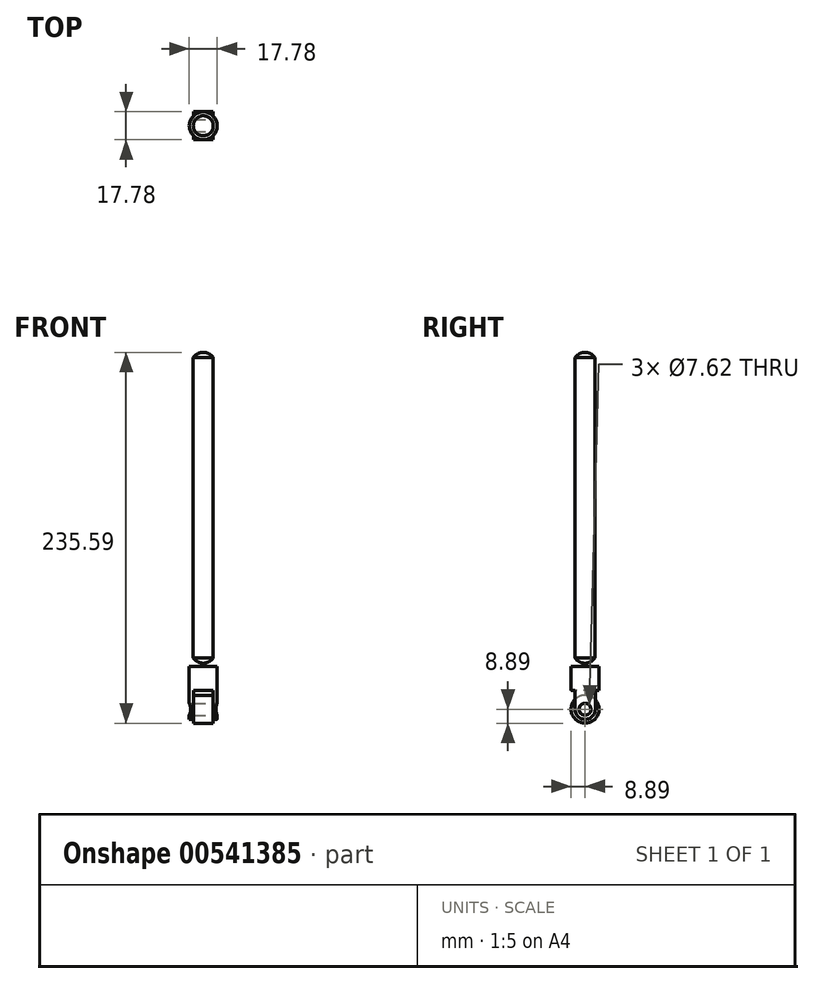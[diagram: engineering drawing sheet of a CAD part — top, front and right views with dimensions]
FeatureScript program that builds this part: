
annotation { "Feature Type Name" : "Feature", "Feature Type Description" : "" }
export const myFeature = defineFeature(function(context is Context, id is Id, definition is map)
    precondition{}
    {
        {
            var Q0;
            Q0=qCreatedBy(makeId("Top.planeOp"),FACE);
            var sketch = newSketch(context, id + "F0", { "sketchPlane" : qUnion([Q0])});
            skCircle(sketch, "E0", {"center": v(0, 0) * mm, "radius": 8.9 * mm});
            skSolve(sketch);
        }
        {
            var Q0;
            Q0=makeQuery(id+"F0.imprint","IMPRINT",FACE,{"disambiguationData":[TD([[makeQuery(id+"F0.imprint","IMPRINT",EDGE,{"derivedFrom":sQuery(id+"F0.wireOp",EDGE,"E0")}),1.0]])]});
            extrude(context, id + "F1", {"entities" : qUnion([Q0]), "depth" : 38.1 * mm, "offsetDistance" : 25.4 * mm});
        }
        {
            var Q0;
            Q0=qCreatedBy(makeId("Right.planeOp"),FACE);
            cPlane(context, id + "F2", {"entities" : qUnion([Q0]), "cplaneType" : CPlaneType.OFFSET, "offset" : 25.4 * mm, "width" : 152.4 * mm, "height" : 152.4 * mm});
        }
        {
            var Q0;
            Q0=qCreatedBy(id+"F2.planeOp",FACE);
            var sketch = newSketch(context, id + "F3", { "sketchPlane" : qUnion([Q0])});
            skArc(sketch, "E1", {"start": v(-6.46, 8.9) * mm, "mid": v(0, 2.43) * mm, "end": v(6.46, 8.9) * mm});
            skLineSegment(sketch, "E2", {"start": v(-6.46, 8.9) * mm, "end": v(-6.46, 16.75) * mm});
            skLineSegment(sketch, "E3", {"start": v(-6.46, 16.75) * mm, "end": v(-10.05, 18.03) * mm});
            skLineSegment(sketch, "E4", {"start": v(-10.05, 18.03) * mm, "end": v(-10.05, 27.68) * mm});
            skLineSegment(sketch, "E5", {"start": v(-10.05, 27.68) * mm, "end": v(-15.58, 29.5) * mm});
            skLineSegment(sketch, "E6", {"start": v(-15.58, 29.5) * mm, "end": v(-19.3, -10.06) * mm});
            skLineSegment(sketch, "E7", {"start": v(-19.3, -10.06) * mm, "end": v(0, -10.06) * mm});
            skLineSegment(sketch, "E8.MirrorCS", {"start": v(19.3, -10.06) * mm, "end": v(0, -10.06) * mm});
            skLineSegment(sketch, "E9.MirrorCS", {"start": v(15.58, 29.5) * mm, "end": v(19.3, -10.06) * mm});
            skLineSegment(sketch, "E10.MirrorCS", {"start": v(6.46, 8.9) * mm, "end": v(6.46, 16.75) * mm});
            skLineSegment(sketch, "E11.MirrorCS", {"start": v(6.46, 16.75) * mm, "end": v(10.05, 18.03) * mm});
            skLineSegment(sketch, "E12.MirrorCS", {"start": v(10.05, 18.03) * mm, "end": v(10.05, 27.68) * mm});
            skLineSegment(sketch, "E13.MirrorCS", {"start": v(10.05, 27.68) * mm, "end": v(15.58, 29.5) * mm});
            skSolve(sketch);
        }
        {
            var Q0;
            Q0=makeQuery(id+"F3.imprint","IMPRINT",FACE,{"disambiguationData":[TD([[makeQuery(id+"F3.imprint","IMPRINT",EDGE,{"derivedFrom":sQuery(id+"F3.wireOp",EDGE,"E1")}),-1.0]])]});
            extrude(context, id + "F4", {"entities" : qUnion([Q0]), "operationType" : NewBodyOperationType.REMOVE, "oppositeDirection" : true, "depth" : 38.25 * mm, "offsetDistance" : 25.4 * mm});
        }
        {
            var Q0;
            Q0=makeQuery(id+"F4.boolean.opBoolean","COPY",FACE,{"derivedFrom":makeQuery(id+"F4.opExtrude","SWEPT_FACE",FACE,{"disambiguationData":[OSD([sQuery(id+"F3.wireOp",EDGE,"E2")])]})});
            cPlane(context, id + "F5", {"entities" : qUnion([Q0]), "cplaneType" : CPlaneType.OFFSET, "offset" : 25.4 * mm, "width" : 152.4 * mm, "height" : 152.4 * mm});
        }
        {
            var Q0;
            Q0=qCreatedBy(id+"F5.planeOp",FACE);
            var sketch = newSketch(context, id + "F6", { "sketchPlane" : qUnion([Q0])});
            skLineSegment(sketch, "E14", {"start": v(6.11, 8.9) * mm, "end": v(6.11, 16.75) * mm});
            skLineSegment(sketch, "E15", {"start": v(-6.11, 16.75) * mm, "end": v(-6.11, -8.4) * mm});
            skLineSegment(sketch, "E16", {"start": v(6.11, -8.4) * mm, "end": v(-6.11, -8.4) * mm});
            skLineSegment(sketch, "E17", {"start": v(6.11, -8.4) * mm, "end": v(6.11, 8.9) * mm});
            skLineSegment(sketch, "E18", {"start": v(6.11, 16.75) * mm, "end": v(6.11, 20.88) * mm});
            skLineSegment(sketch, "E19", {"start": v(-6.11, 20.88) * mm, "end": v(6.11, 20.88) * mm});
            skLineSegment(sketch, "E20", {"start": v(-6.11, 20.88) * mm, "end": v(-6.11, 16.75) * mm});
            skSolve(sketch);
        }
        {
            var Q0;
            Q0=makeQuery(id+"F6.imprint","IMPRINT",FACE,{"disambiguationData":[TD([[makeQuery(id+"F6.imprint","IMPRINT",EDGE,{"derivedFrom":sQuery(id+"F6.wireOp",EDGE,"E14")}),1.0]])]});
            var Q1;
            {var subQ2=sQuery(id+"F6.wireOp",EDGE,"E16");Q1=makeQuery(id+"F6.imprint","IMPRINT",FACE,{"disambiguationData":[TD([[makeQuery(id+"F6.imprint","IMPRINT",EDGE,{"derivedFrom":subQ2}),-1.0]])]});}
            extrude(context, id + "F7", {"entities" : qUnion([Q0, Q1]), "operationType" : NewBodyOperationType.REMOVE, "oppositeDirection" : true, "depth" : 48.8 * mm, "offsetDistance" : 25.4 * mm});
        }
        {
            var Q0;
            Q0=makeQuery(id+"F7.boolean.opBoolean","COPY",FACE,{"derivedFrom":makeQuery(id+"F7.opExtrude","SWEPT_FACE",FACE,{"disambiguationData":[OSD([sQuery(id+"F6.wireOp",EDGE,"E14"),sQuery(id+"F6.wireOp",EDGE,"E17")])]})});
            var sketch = newSketch(context, id + "F8", { "sketchPlane" : qUnion([Q0])});
            skCircle(sketch, "E21", {"center": v(0, 8.9) * mm, "radius": 3.81 * mm});
            skSolve(sketch);
        }
        {
            var Q0;
            Q0=makeQuery(id+"F8.imprint","IMPRINT",FACE,{"disambiguationData":[TD([[makeQuery(id+"F8.imprint","IMPRINT",EDGE,{"derivedFrom":sQuery(id+"F8.wireOp",EDGE,"E21")}),1.0]])]});
            extrude(context, id + "F9", {"entities" : qUnion([Q0]), "operationType" : NewBodyOperationType.REMOVE, "endBound" : BoundingType.SYMMETRIC, "depth" : 113.28 * mm, "offsetDistance" : 25.4 * mm});
        }
        {
            var Q0;
            Q0=makeQuery(id+"F7.boolean.opBoolean","COPY",FACE,{"derivedFrom":makeQuery(id+"F7.opExtrude","SWEPT_FACE",FACE,{"disambiguationData":[OSD([sQuery(id+"F6.wireOp",EDGE,"E14"),sQuery(id+"F6.wireOp",EDGE,"E17")])]})});
            var sketch = newSketch(context, id + "F10", { "sketchPlane" : qUnion([Q0])});
            skCircle(sketch, "E22", {"center": v(0, 8.9) * mm, "radius": 8.9 * mm});
            skCircle(sketch, "E23", {"center": v(0, 8.9) * mm, "radius": 3.81 * mm});
            skSolve(sketch);
        }
        {
            var Q0;
            Q0=makeQuery(id+"F10.imprint","IMPRINT",FACE,{"disambiguationData":[TD([[makeQuery(id+"F10.imprint","IMPRINT",EDGE,{"derivedFrom":sQuery(id+"F10.wireOp",EDGE,"E23")}),-1.0]])]});
            var Q1;
            {var subQ1=makeQuery(id+"F7.opExtrude","SWEPT_FACE",FACE,{"disambiguationData":[OSD([sQuery(id+"F6.wireOp",EDGE,"E14"),sQuery(id+"F6.wireOp",EDGE,"E17"),sQuery(id+"F6.wireOp",EDGE,"E18")])]});var subQ7=makeQuery(id+"F7.boolean.opBoolean","INTERSECT",EDGE,{"derivedFrom":[makeQuery(id+"F4.boolean.opBoolean","COPY",FACE,{"derivedFrom":makeQuery(id+"F4.opExtrude","SWEPT_FACE",FACE,{"disambiguationData":[OSD([sQuery(id+"F3.wireOp",EDGE,"E1")])]})}),subQ1]});Q1=makeQuery(id+"F10.imprint","IMPRINT",FACE,{"disambiguationData":[TD([[makeQuery(id+"F10.imprint","IMPRINT",EDGE,{"derivedFrom":subQ7}),-1.0]])]});}
            var Q2;
            Q2=makeQuery(id+"F7.boolean.opBoolean","COPY",FACE,{"derivedFrom":makeQuery(id+"F7.opExtrude","SWEPT_FACE",FACE,{"disambiguationData":[OSD([sQuery(id+"F6.wireOp",EDGE,"E15"),sQuery(id+"F6.wireOp",EDGE,"E20")])]})});
            extrude(context, id + "F11", {"entities" : qUnion([Q0, Q1]), "endBound" : BoundingType.UP_TO_SURFACE, "depth" : 25.4 * mm, "endBoundEntityFace" : qUnion([Q2]), "offsetDistance" : 25.4 * mm});
        }
        {
            var Q0;
            Q0=makeQuery(id+"F1.opExtrude","CAP_FACE",FACE,{"disambiguationData":[OSD([sQuery(id+"F0.wireOp",EDGE,"E0")])],"isStart":false});
            var sketch = newSketch(context, id + "F12", { "sketchPlane" : qUnion([Q0])});
            skCircle(sketch, "E24", {"center": v(0, 0) * mm, "radius": 6.35 * mm});
            skSolve(sketch);
        }
        {
            var Q0;
            Q0=makeQuery(id+"F12.imprint","IMPRINT",FACE,{"disambiguationData":[TD([[makeQuery(id+"F12.imprint","IMPRINT",EDGE,{"derivedFrom":sQuery(id+"F12.wireOp",EDGE,"E24")}),1.0]])]});
            extrude(context, id + "F13", {"entities" : qUnion([Q0]), "depth" : 197.48 * mm, "offsetDistance" : 25.4 * mm});
        }
        {
            var Q0;
            Q0=qCreatedBy(makeId("Right.planeOp"),FACE);
            var sketch = newSketch(context, id + "F14", { "sketchPlane" : qUnion([Q0])});
            skCircle(sketch, "E25", {"center": v(0, 45.72) * mm, "radius": 7.62 * mm});
            skLineSegment(sketch, "E26", {"start": v(-7.62, 45.72) * mm, "end": v(-9.1, 45.72) * mm});
            skLineSegment(sketch, "E27", {"start": v(-9.1, 45.72) * mm, "end": v(-9.1, 36.06) * mm});
            skLineSegment(sketch, "E28", {"start": v(-9.1, 36.06) * mm, "end": v(0, 36.06) * mm});
            skLineSegment(sketch, "E29", {"start": v(0, 36.06) * mm, "end": v(13.28, 36.06) * mm});
            skLineSegment(sketch, "E30", {"start": v(13.28, 36.06) * mm, "end": v(12.18, 45.72) * mm});
            skLineSegment(sketch, "E31", {"start": v(12.18, 45.72) * mm, "end": v(7.62, 45.72) * mm});
            skLineSegment(sketch, "E32", {"start": v(0, 45.72) * mm, "end": v(0, 31.62) * mm});
            skLineSegment(sketch, "E33", {"start": v(0, 45.72) * mm, "end": v(0, 53.34) * mm});
            skSolve(sketch);
        }
        {
            var Q0;
            {var subQ1=sQuery(id+"F14.wireOp",EDGE,"E26");Q0=makeQuery(id+"F14.imprint","IMPRINT",FACE,{"disambiguationData":[TD([[makeQuery(id+"F14.imprint","IMPRINT",EDGE,{"derivedFrom":subQ1}),1.0]])]});}
            var Q1;
            Q1=sQuery(id+"F14.wireOp",EDGE,"E33");
            revolve(context, id + "F15", {"operationType" : NewBodyOperationType.REMOVE, "entities" : qUnion([Q0]), "axis" : qUnion([Q1]), "revolveType" : RevolveType.FULL, "oppositeDirection" : true});
        }
        {
            var Q0;
            Q0=qCreatedBy(makeId("Right.planeOp"),FACE);
            var sketch = newSketch(context, id + "F16", { "sketchPlane" : qUnion([Q0])});
            skArc(sketch, "E34", {"start": v(-7.6, 227.47) * mm, "mid": v(5.56, 222.75) * mm, "end": v(0, 235.59) * mm});
            skLineSegment(sketch, "E35", {"start": v(0, 220.35) * mm, "end": v(0, 227.97) * mm});
            skLineSegment(sketch, "E36", {"start": v(0, 227.97) * mm, "end": v(0, 245.81) * mm});
            skLineSegment(sketch, "E37", {"start": v(0, 245.81) * mm, "end": v(-18.55, 245.81) * mm});
            skLineSegment(sketch, "E38", {"start": v(-18.55, 245.81) * mm, "end": v(-16.75, 225.78) * mm});
            skLineSegment(sketch, "E39", {"start": v(-16.75, 225.78) * mm, "end": v(-7.6, 227.47) * mm});
            skCircle(sketch, "E40", {"center": v(0, 227.97) * mm, "radius": 7.62 * mm});
            skSolve(sketch);
        }
        {
            var Q0;
            {var subQ1=sQuery(id+"F16.wireOp",EDGE,"E37");Q0=makeQuery(id+"F16.imprint","IMPRINT",FACE,{"disambiguationData":[TD([[makeQuery(id+"F16.imprint","IMPRINT",EDGE,{"derivedFrom":subQ1}),1.0]])]});}
            var Q1;
            Q1=sQuery(id+"F16.wireOp",EDGE,"E36");
            revolve(context, id + "F17", {"operationType" : NewBodyOperationType.REMOVE, "entities" : qUnion([Q0]), "axis" : qUnion([Q1]), "revolveType" : RevolveType.FULL, "oppositeDirection" : true});
        }
    });
